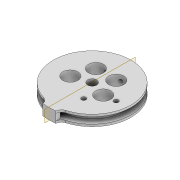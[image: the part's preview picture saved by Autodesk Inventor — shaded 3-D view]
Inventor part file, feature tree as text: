
AUTODESK INVENTOR PART (.ipt)
format: ipt  version: 2022 (Build 260153000, 153)  size: 301,568 bytes
history: native  units: mm
features: extrude x8, sketch x7, plane x3, fillet x2, pattern_circular x1, mirror x1, projected_geometry x1
ambient origin geometry x8: Origin, YZ Plane, XZ Plane, XY Plane, X Axis, Y Axis, Z Axis, Center Point
bodies: Solid1 (feature_tree)
feature tree (23):
  extrude  "Extrusion1"  Depth=30.0mm
  extrude  "Extrusion2"  Depth=3.0mm TaperAngle=0.0deg
  pattern_circular  "Circular Pattern1"  Count=5 Angle=360.0deg
  plane  "Work Plane1"
  plane  "Work Plane2"
  extrude  "Extrusion3"  [1 undecoded]
  extrude  "Extrusion4"  Depth=3.0mm
  fillet  "Fillet1"  Radius=1.7mm
  plane  "Work Plane3"
  extrude  "Extrusion5"  Depth=10.0mm TaperAngle=0.0deg
  mirror  "Mirror1"
  sketch  "Sketch6"  dims[d13=9.599311mm d14=-9.599311mm]
  extrude  "Extrusion6"  Depth=3.0mm
  extrude  "Extrusion7"  Depth=3.0mm
  extrude  "Extrusion8"  Depth=3.0mm
  fillet  "Fillet2"  Radius=10.0mm
  sketch  "Sketch1"  dims[d0=4.2mm d2=30.0mm]
  sketch  "Sketch2"  dims[d3=4.0mm d4=3.0mm d5=0.0mm]
  sketch  "Sketch3"  dims[d6=7.0mm]
  sketch  "Sketch4"  dims[d7=8.0mm]
  sketch  "Sketch5"  dims[d8=10.0mm d9=0.0mm d10=50.0mm d11=360.0deg]
  projected_geometry  "Projected Loop1"
  sketch  "Sketch7"  dims[d15=1.5mm d16=1.5mm d17=1.7mm d18=10.0mm d19=0.0mm d20=1.5mm d21=1.5mm d22=1.7mm d23=10.0mm d24=0.0mm d25=1.0mm d26=36.0mm d27=1.0mm d28=0.0mm d29=2.1mm d30=13.0mm d31=1.9mm d32=2.1mm d33=8.4mm d35=5.0mm d36=0.0mm d37=100.0mm d38=0.0mm d39=4.5mm d40=3.0mm d41=3.0mm d42=2.0mm d43=5.0mm d44=0.0mm d45=3.0mm]
note: 1 required parameter value undecoded (feature->parameter linkage not recoverable at this tier; creation-order binding heuristic only, values carry confidence <= 0.55)
